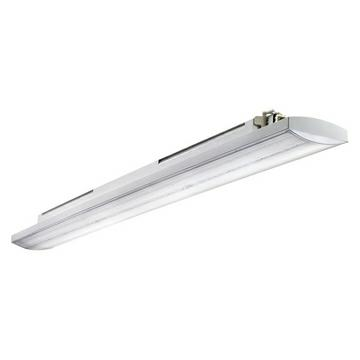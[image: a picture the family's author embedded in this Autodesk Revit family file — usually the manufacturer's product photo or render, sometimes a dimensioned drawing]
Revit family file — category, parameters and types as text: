
# Revit family: Lighting-Industriale-GEWISS-SMART[3]-PLAFONIERA-LED_TRASPARENTE_1600mm
name_source: partatom
category: Apparecchi per illuminazione
units: mm (PartAtom-declared; Revit-internal decimal feet)

## family parameters
Condiviso = No
Host = Superficie
Punto di calcolo locali = Sì
Quota connettore circolare = Usa diametro
Sorgente d'illuminazione = No
Taglio con vuoti quando caricato = No
Tipo di parte = Normale

## types (1)
- Lighting-Industriale-GEWISS-SMART[3]-PLAFONIERA-LED_TRASPARENTE_1600mm
    Apparecchio a ridotta temperatura superficiale = Conforme
    Applicazione = Interno
    Catalogo = LIGHTING
    Catalogo Serie = SMART [3]
    Classe di efficienza LED integrati = A ÷ A++
    Classe isolamento = II
    Codice EAN = 8011564869141
    Codice Electrocod = 2434
    Descrizione = SMART3 1600 72LED 27W TRASPARENTE DALI 4000K
    Failure rate apparecchio (35.000h, Tq=35° C) = <2,5%
    Failure rate apparecchio (50.000h, Tq=25° C) = <2,5%
    Flusso nominale (lm) = 3700
    Ganci = GEWISS  - ALLUMINIO
    Garanzia = 5 anni
    Glow Wire Test = 850°C
    Grado di protezione = IP66/IP69
    IDF = ec075b24-a116-4a18-9c14-fe6cdf187fcb
    IDT = fad509ce-101b-4a7a-befe-b015b7d6ede8
    Immagine tipo = GWS3158T.jpg
    LED Life time (L70) = 80000H
    LED Life time (L80B50) = 100000H
    LED Life time (L90B50) = 50000H
    LED LifeTime (L80B20) = 85000H
    Lampada = LED
    Lampada: = LED
    Lumen output (lm) = 3400
    Lunghezza = 1600 mm
    Lunghezza Lampada = 1600 mm  [stored 5.24934 ft]
    Modello = GWS3158TD
    N° LED (#) = 72
    Peso (kg): = 2,5
    Potenza di sistema = 26W
    Produttore = GEWISS S.p.A.
    Prospetto di default = 1219 mm
    Resistenza agli urti = IK08
    SEO = Plafoniera
    Scheda Tecnica = https://www.gewiss.com
    Schermo = Trasparente
    Schermo- = Gewiss - Led Acceso
    Stampa 1_100 = Sì
    Stampa 1_200 = No
    Struttura = GEWISS - SMART 3 - GRIGIO
    Temperatura di colore = 4000 K (CRI 80)
    Temperatura di colore: = 4000 K (CRI 80)
    Temperatura di funzionamento = -25 +50 °C
    Temperatura di utilizzo = -30 +50 °C
    Tensione = 220/240 V - 50/60 Hz - Dali
    Tipo alimentatore = Driver Led in corrente continua
    Tipologia = DALI
    Tipologia sorgente luminosa = LED - Non sostituibile
    URL = https://www.gewiss.com
    Versione file RFA = 20.11

note: [stored X ft] marks values corroborated as IEEE doubles in the binary element streams (Revit-internal decimal feet)
